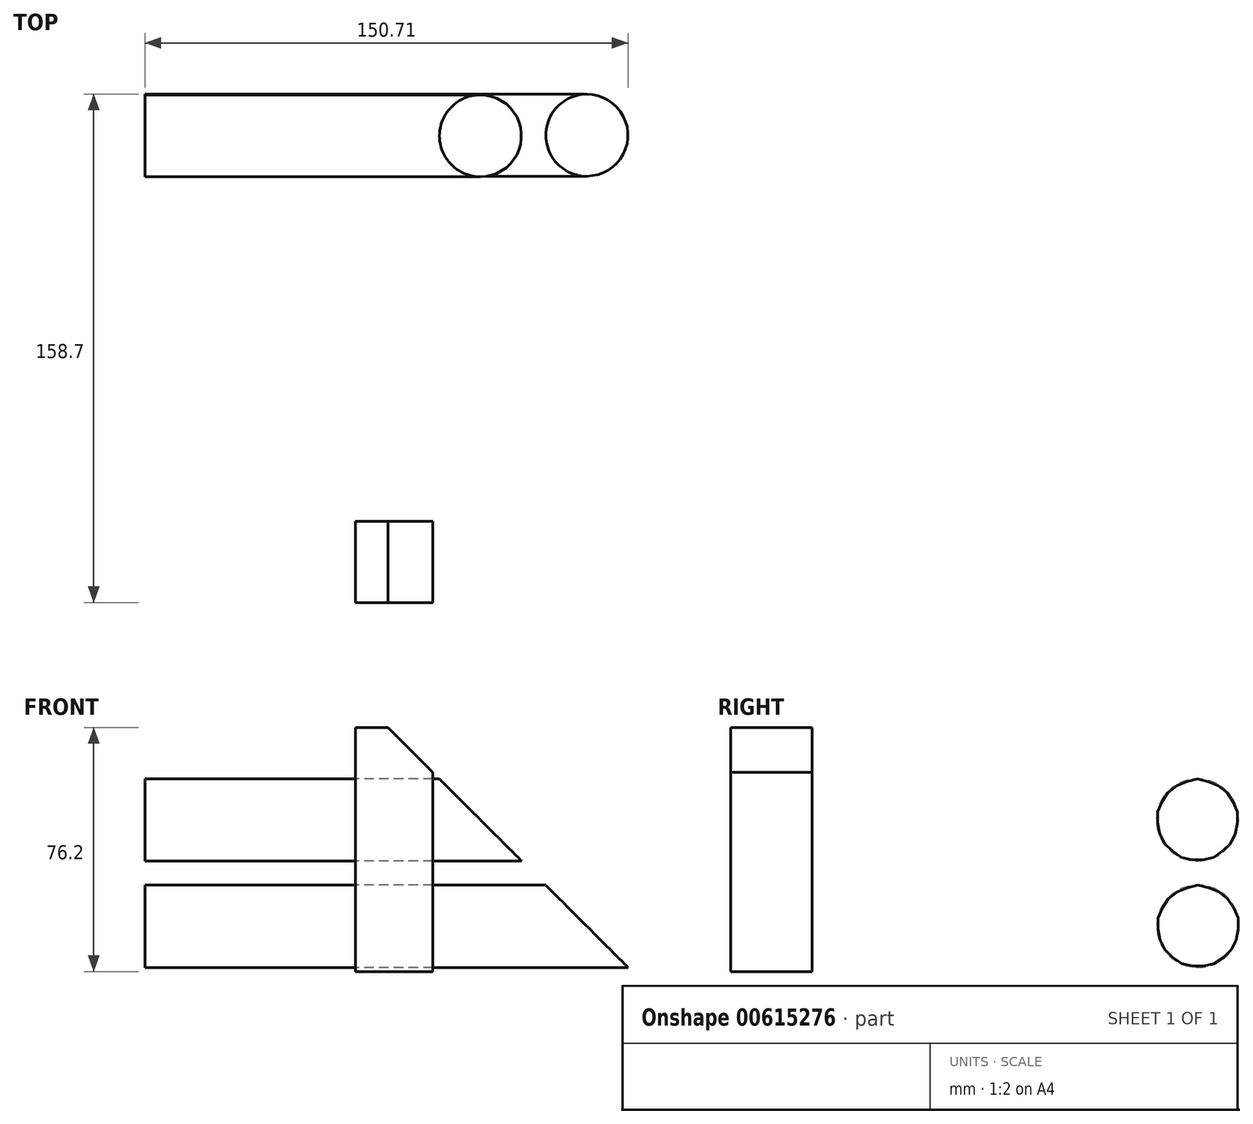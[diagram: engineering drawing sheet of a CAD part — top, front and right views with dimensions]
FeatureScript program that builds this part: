
annotation { "Feature Type Name" : "Feature", "Feature Type Description" : "" }
export const myFeature = defineFeature(function(context is Context, id is Id, definition is map)
    precondition{}
    {
        {
            var Q0;
            Q0=qCreatedBy(makeId("Top.planeOp"),FACE);
            var sketch = newSketch(context, id + "F0", { "sketchPlane" : qUnion([Q0])});
            skLineSegment(sketch, "E0.bottom", {"start": v(-75.75, -75.21) * mm, "end": v(76.25, -75.21) * mm});
            skLineSegment(sketch, "E0.top", {"start": v(-75.75, 75.5) * mm, "end": v(76.25, 75.5) * mm});
            skLineSegment(sketch, "E0.left", {"start": v(-75.75, -75.21) * mm, "end": v(-75.75, 75.5) * mm});
            skLineSegment(sketch, "E0.right", {"start": v(76.25, -75.21) * mm, "end": v(76.25, 75.5) * mm});
            skSolve(sketch);
        }
        {
            var Q0;
            Q0=makeQuery(id+"F0.imprint","IMPRINT",FACE,{"disambiguationData":[TD([[makeQuery(id+"F0.imprint","IMPRINT",EDGE,{"derivedFrom":sQuery(id+"F0.wireOp",EDGE,"E0.bottom")}),1.0]])]});
            extrude(context, id + "F1", {"entities" : qUnion([Q0]), "depth" : 76.2 * mm, "offsetDistance" : 25.4 * mm});
        }
        {
            var Q0;
            Q0=makeQuery(id+"F1.opExtrude","SWEPT_FACE",FACE,{"disambiguationData":[OSD([sQuery(id+"F0.wireOp",EDGE,"E0.bottom")])]});
            var sketch = newSketch(context, id + "F2", { "sketchPlane" : qUnion([Q0])});
            skLineSegment(sketch, "E1", {"start": v(0, 76.2) * mm, "end": v(76.25, 0) * mm});
            skLineSegment(sketch, "E2", {"start": v(76.25, 0) * mm, "end": v(76.25, 76.2) * mm});
            skLineSegment(sketch, "E3", {"start": v(76.25, 76.2) * mm, "end": v(0, 76.2) * mm});
            skSolve(sketch);
        }
        {
            var Q0;
            Q0=makeQuery(id+"F2.imprint","IMPRINT",FACE,{"disambiguationData":[TD([[makeQuery(id+"F2.imprint","IMPRINT",EDGE,{"derivedFrom":sQuery(id+"F2.wireOp",EDGE,"E1")}),1.0]])]});
            extrude(context, id + "F3", {"entities" : qUnion([Q0]), "operationType" : NewBodyOperationType.REMOVE, "oppositeDirection" : true, "depth" : 76.2 * mm, "offsetDistance" : 25.4 * mm});
        }
        {
            var Q0;
            Q0=makeQuery(id+"F3.boolean.opBoolean","COPY",FACE,{"derivedFrom":makeQuery(id+"F3.opExtrude","CAP_FACE",FACE,{"disambiguationData":[OSD([sQuery(id+"F2.wireOp",EDGE,"E1"),sQuery(id+"F2.wireOp",EDGE,"E2"),sQuery(id+"F2.wireOp",EDGE,"E3")])],"isStart":false})});
            extrude(context, id + "F4", {"entities" : qUnion([Q0]), "operationType" : NewBodyOperationType.REMOVE, "oppositeDirection" : true, "depth" : 1270 * mm, "offsetDistance" : 25.4 * mm});
        }
        {
            var Q0;
            Q0=makeQuery(id+"F1.opExtrude","SWEPT_FACE",FACE,{"disambiguationData":[OSD([sQuery(id+"F0.wireOp",EDGE,"E0.bottom")])]});
            var sketch = newSketch(context, id + "F5", { "sketchPlane" : qUnion([Q0])});
            skLineSegment(sketch, "E4.bottom", {"start": v(-10.15, 76.2) * mm, "end": v(14.05, 76.2) * mm});
            skLineSegment(sketch, "E4.top", {"start": v(-10.15, 0) * mm, "end": v(14.05, 0) * mm});
            skLineSegment(sketch, "E4.left", {"start": v(-10.15, 76.2) * mm, "end": v(-10.15, 0) * mm});
            skLineSegment(sketch, "E4.right", {"start": v(14.05, 76.2) * mm, "end": v(14.05, 0) * mm});
            skSolve(sketch);
        }
        {
            var Q0;
            {var subQ1=sQuery(id+"F5.wireOp",EDGE,"E4.top");Q0=makeQuery(id+"F5.imprint","IMPRINT",FACE,{"disambiguationData":[TD([[makeQuery(id+"F5.imprint","IMPRINT",EDGE,{"derivedFrom":subQ1}),1.0]])]});}
            extrude(context, id + "F6", {"entities" : qUnion([Q0]), "operationType" : NewBodyOperationType.ADD, "depth" : 25.4 * mm, "offsetDistance" : 25.4 * mm});
        }
        {
            var Q0;
            Q0=makeQuery(id+"F1.opExtrude","SWEPT_FACE",FACE,{"disambiguationData":[OSD([sQuery(id+"F0.wireOp",EDGE,"E0.left")])]});
            var sketch = newSketch(context, id + "F7", { "sketchPlane" : qUnion([Q0])});
            skLineSegment(sketch, "E5.bottom", {"start": v(-12.45, 76.2) * mm, "end": v(12.45, 76.2) * mm});
            skLineSegment(sketch, "E5.top", {"start": v(-12.45, 57.6) * mm, "end": v(12.45, 57.6) * mm});
            skLineSegment(sketch, "E5.left", {"start": v(-12.45, 76.2) * mm, "end": v(-12.45, 57.6) * mm});
            skLineSegment(sketch, "E5.right", {"start": v(12.45, 76.2) * mm, "end": v(12.45, 57.6) * mm});
            skPoint(sketch, "E5.middle", {"position": v(0, 66.9) * mm});
            skSolve(sketch);
        }
        {
            var Q0;
            Q0=makeQuery(id+"F7.imprint","IMPRINT",FACE,{"disambiguationData":[TD([[makeQuery(id+"F7.imprint","IMPRINT",EDGE,{"derivedFrom":sQuery(id+"F7.wireOp",EDGE,"E5.bottom")}),1.0]])]});
            extrude(context, id + "F8", {"entities" : qUnion([Q0]), "operationType" : NewBodyOperationType.REMOVE, "oppositeDirection" : true, "depth" : 1270 * mm, "offsetDistance" : 25.4 * mm});
        }
        {
            var Q0;
            Q0=makeQuery(id+"F1.opExtrude","SWEPT_FACE",FACE,{"disambiguationData":[OSD([sQuery(id+"F0.wireOp",EDGE,"E0.left")])]});
            var sketch = newSketch(context, id + "F9", { "sketchPlane" : qUnion([Q0])});
            skLineSegment(sketch, "E6", {"start": v(-75.5, 47.3) * mm, "end": v(75.21, 47.3) * mm});
            skLineSegment(sketch, "E7", {"start": v(-75.5, 14.11) * mm, "end": v(75.21, 14.11) * mm});
            skCircle(sketch, "E8", {"center": v(-45.08, 47.3) * mm, "radius": 12.8 * mm});
            skCircle(sketch, "E9", {"center": v(-45.26, 14.11) * mm, "radius": 12.83 * mm});
            skCircle(sketch, "E10", {"center": v(45.47, 47.3) * mm, "radius": 12.84 * mm});
            skCircle(sketch, "E11", {"center": v(45.47, 14.11) * mm, "radius": 12.92 * mm});
            skSolve(sketch);
        }
        {
            var Q0;
            {var subQ0=sQuery(id+"F9.wireOp",EDGE,"E8");var subQ1=sQuery(id+"F9.wireOp",EDGE,"E6");var subQ2=makeQuery(id+"F9.imprint","INTERSECT",VERTEX,{"disambiguationData":[OD(0.0)],"derivedFrom":[subQ1,subQ0]});Q0=makeQuery(id+"F9.imprint","IMPRINT",FACE,{"disambiguationData":[TD([[makeQuery(id+"F9.imprint","IMPRINT",EDGE,{"disambiguationData":[TD([[subQ2,-1.0]])],"derivedFrom":subQ1}),1.0]])]});}
            var Q1;
            {var subQ0=sQuery(id+"F9.wireOp",EDGE,"E8");var subQ1=sQuery(id+"F9.wireOp",EDGE,"E6");var subQ2=makeQuery(id+"F9.imprint","INTERSECT",VERTEX,{"disambiguationData":[OD(0.0)],"derivedFrom":[subQ1,subQ0]});Q1=makeQuery(id+"F9.imprint","IMPRINT",FACE,{"disambiguationData":[TD([[makeQuery(id+"F9.imprint","IMPRINT",EDGE,{"disambiguationData":[TD([[subQ2,-1.0]])],"derivedFrom":subQ1}),-1.0]])]});}
            var Q2;
            {var subQ0=sQuery(id+"F9.wireOp",EDGE,"E9");var subQ1=sQuery(id+"F9.wireOp",EDGE,"E7");var subQ2=makeQuery(id+"F9.imprint","INTERSECT",VERTEX,{"disambiguationData":[OD(0.0)],"derivedFrom":[subQ1,subQ0]});Q2=makeQuery(id+"F9.imprint","IMPRINT",FACE,{"disambiguationData":[TD([[makeQuery(id+"F9.imprint","IMPRINT",EDGE,{"disambiguationData":[TD([[subQ2,-1.0]])],"derivedFrom":subQ1}),1.0]])]});}
            var Q3;
            {var subQ0=sQuery(id+"F9.wireOp",EDGE,"E9");var subQ1=sQuery(id+"F9.wireOp",EDGE,"E7");var subQ2=makeQuery(id+"F9.imprint","INTERSECT",VERTEX,{"disambiguationData":[OD(0.0)],"derivedFrom":[subQ1,subQ0]});Q3=makeQuery(id+"F9.imprint","IMPRINT",FACE,{"disambiguationData":[TD([[makeQuery(id+"F9.imprint","IMPRINT",EDGE,{"disambiguationData":[TD([[subQ2,-1.0]])],"derivedFrom":subQ1}),-1.0]])]});}
            var Q4;
            {var subQ0=sQuery(id+"F9.wireOp",EDGE,"E11");var subQ1=sQuery(id+"F9.wireOp",EDGE,"E7");var subQ2=makeQuery(id+"F9.imprint","INTERSECT",VERTEX,{"disambiguationData":[OD(0.0)],"derivedFrom":[subQ1,subQ0]});Q4=makeQuery(id+"F9.imprint","IMPRINT",FACE,{"disambiguationData":[TD([[makeQuery(id+"F9.imprint","IMPRINT",EDGE,{"disambiguationData":[TD([[subQ2,-1.0]])],"derivedFrom":subQ1}),-1.0]])]});}
            var Q5;
            {var subQ0=sQuery(id+"F9.wireOp",EDGE,"E11");var subQ1=sQuery(id+"F9.wireOp",EDGE,"E7");var subQ2=makeQuery(id+"F9.imprint","INTERSECT",VERTEX,{"disambiguationData":[OD(0.0)],"derivedFrom":[subQ1,subQ0]});Q5=makeQuery(id+"F9.imprint","IMPRINT",FACE,{"disambiguationData":[TD([[makeQuery(id+"F9.imprint","IMPRINT",EDGE,{"disambiguationData":[TD([[subQ2,-1.0]])],"derivedFrom":subQ1}),1.0]])]});}
            var Q6;
            {var subQ0=sQuery(id+"F9.wireOp",EDGE,"E10");var subQ1=sQuery(id+"F9.wireOp",EDGE,"E6");var subQ2=makeQuery(id+"F9.imprint","INTERSECT",VERTEX,{"disambiguationData":[OD(0.0)],"derivedFrom":[subQ1,subQ0]});Q6=makeQuery(id+"F9.imprint","IMPRINT",FACE,{"disambiguationData":[TD([[makeQuery(id+"F9.imprint","IMPRINT",EDGE,{"disambiguationData":[TD([[subQ2,-1.0]])],"derivedFrom":subQ1}),-1.0]])]});}
            var Q7;
            {var subQ0=sQuery(id+"F9.wireOp",EDGE,"E10");var subQ1=sQuery(id+"F9.wireOp",EDGE,"E6");var subQ2=makeQuery(id+"F9.imprint","INTERSECT",VERTEX,{"disambiguationData":[OD(0.0)],"derivedFrom":[subQ1,subQ0]});Q7=makeQuery(id+"F9.imprint","IMPRINT",FACE,{"disambiguationData":[TD([[makeQuery(id+"F9.imprint","IMPRINT",EDGE,{"disambiguationData":[TD([[subQ2,-1.0]])],"derivedFrom":subQ1}),1.0]])]});}
            extrude(context, id + "F10", {"entities" : qUnion([Q0, Q1, Q2, Q3, Q4, Q5, Q6, Q7]), "operationType" : NewBodyOperationType.REMOVE, "endBound" : BoundingType.THROUGH_ALL, "oppositeDirection" : true, "depth" : 25.4 * mm, "offsetDistance" : 25.4 * mm});
        }
    });
